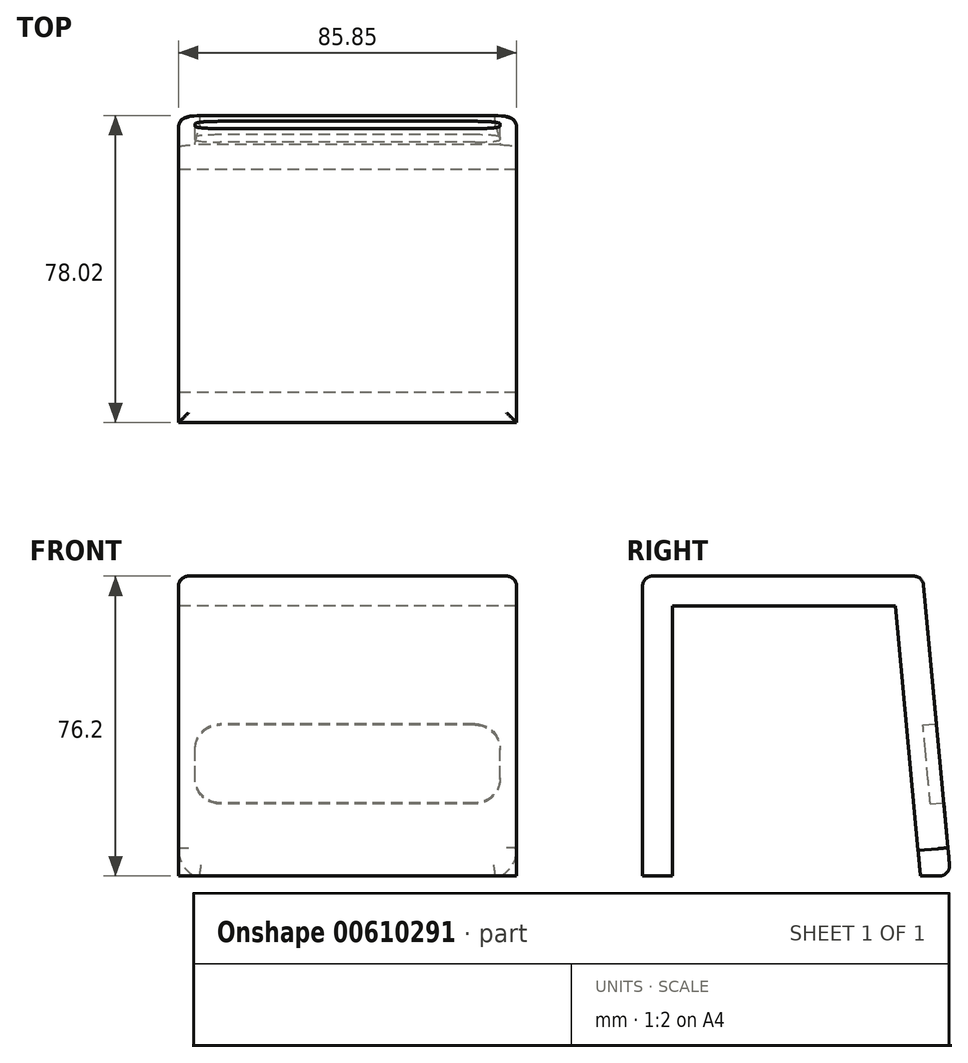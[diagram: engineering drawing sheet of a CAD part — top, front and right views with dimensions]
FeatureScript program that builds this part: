
annotation { "Feature Type Name" : "Feature", "Feature Type Description" : "" }
export const myFeature = defineFeature(function(context is Context, id is Id, definition is map)
    precondition{}
    {
        {
            var Q0;
            Q0=qCreatedBy(makeId("Right.planeOp"),FACE);
            var sketch = newSketch(context, id + "F0", { "sketchPlane" : qUnion([Q0])});
            skLineSegment(sketch, "E0", {"start": v(0, 0) * mm, "end": v(0, 76.2) * mm});
            skLineSegment(sketch, "E1", {"start": v(0, 76.2) * mm, "end": v(71.2, 76.2) * mm});
            skLineSegment(sketch, "E2", {"start": v(71.2, 76.2) * mm, "end": v(78.26, 0) * mm});
            skLineSegment(sketch, "E3", {"start": v(78.26, 0) * mm, "end": v(70.61, 0) * mm});
            skLineSegment(sketch, "E4", {"start": v(70.61, 0) * mm, "end": v(64.26, 68.58) * mm});
            skLineSegment(sketch, "E5", {"start": v(64.26, 68.58) * mm, "end": v(7.62, 68.58) * mm});
            skLineSegment(sketch, "E6", {"start": v(7.62, 68.58) * mm, "end": v(7.62, 0) * mm});
            skLineSegment(sketch, "E7", {"start": v(7.62, 0) * mm, "end": v(0, 0) * mm});
            skSolve(sketch);
        }
        {
            var Q0;
            Q0 = qSketchRegion(id + "F0", true);
            extrude(context, id + "F1", {"entities" : qUnion([Q0]), "depth" : 85.85 * mm, "offsetDistance" : 25.4 * mm});
        }
        {
            var Q0;
            Q0=makeQuery(id+"F1.opExtrude","SWEPT_FACE",FACE,{"disambiguationData":[OSD([sQuery(id+"F0.wireOp",EDGE,"E2")])]});
            var sketch = newSketch(context, id + "F2", { "sketchPlane" : qUnion([Q0])});
            skLineSegment(sketch, "E8.bottom", {"start": v(-75.31, 11.46) * mm, "end": v(-10.54, 11.46) * mm});
            skLineSegment(sketch, "E8.top", {"start": v(-75.31, 31.63) * mm, "end": v(-10.54, 31.63) * mm});
            skLineSegment(sketch, "E8.left", {"start": v(-81.66, 17.81) * mm, "end": v(-81.66, 25.28) * mm});
            skLineSegment(sketch, "E8.right", {"start": v(-4.2, 17.81) * mm, "end": v(-4.2, 25.28) * mm});
            skPoint(sketch, "E9.visualSharp", {"position": v(-4.2, 31.63) * mm});
            skArc(sketch, "E9.filletArc", {"start": v(-4.2, 25.28) * mm, "mid": v(-6.05, 29.77) * mm, "end": v(-10.54, 31.63) * mm});
            skPoint(sketch, "E10.visualSharp", {"position": v(-4.2, 11.46) * mm});
            skArc(sketch, "E10.filletArc", {"start": v(-10.54, 11.46) * mm, "mid": v(-6.05, 13.32) * mm, "end": v(-4.2, 17.81) * mm});
            skPoint(sketch, "E11.visualSharp", {"position": v(-81.66, 11.46) * mm});
            skArc(sketch, "E11.filletArc", {"start": v(-81.66, 17.81) * mm, "mid": v(-79.8, 13.32) * mm, "end": v(-75.31, 11.46) * mm});
            skPoint(sketch, "E12.visualSharp", {"position": v(-81.66, 31.63) * mm});
            skArc(sketch, "E12.filletArc", {"start": v(-75.31, 31.63) * mm, "mid": v(-79.8, 29.77) * mm, "end": v(-81.66, 25.28) * mm});
            skArc(sketch, "E13.0", {"start": v(-75.31, 32.42) * mm, "mid": v(-80.36, 30.33) * mm, "end": v(-82.45, 25.28) * mm});
            skLineSegment(sketch, "E13.1", {"start": v(-82.45, 17.81) * mm, "end": v(-82.45, 25.28) * mm});
            skLineSegment(sketch, "E13.2", {"start": v(-75.31, 32.42) * mm, "end": v(-10.54, 32.42) * mm});
            skArc(sketch, "E13.3", {"start": v(-82.45, 17.81) * mm, "mid": v(-80.36, 12.76) * mm, "end": v(-75.31, 10.67) * mm});
            skArc(sketch, "E13.4", {"start": v(-3.4, 25.28) * mm, "mid": v(-5.49, 30.33) * mm, "end": v(-10.54, 32.42) * mm});
            skLineSegment(sketch, "E13.5", {"start": v(-3.4, 17.81) * mm, "end": v(-3.4, 25.28) * mm});
            skArc(sketch, "E13.6", {"start": v(-10.54, 10.67) * mm, "mid": v(-5.49, 12.76) * mm, "end": v(-3.4, 17.81) * mm});
            skLineSegment(sketch, "E13.7", {"start": v(-75.31, 10.67) * mm, "end": v(-10.54, 10.67) * mm});
            skSolve(sketch);
        }
        {
            var Q0;
            Q0=makeQuery(id+"F2.imprint","IMPRINT",FACE,{"disambiguationData":[TD([[makeQuery(id+"F2.imprint","IMPRINT",EDGE,{"derivedFrom":sQuery(id+"F2.wireOp",EDGE,"E8.bottom")}),1.0]])]});
            extrude(context, id + "F3", {"entities" : qUnion([Q0]), "operationType" : NewBodyOperationType.REMOVE, "oppositeDirection" : true, "depth" : 3.43 * mm, "offsetDistance" : 25.4 * mm});
        }
        {
            var Q0;
            Q0=makeQuery(id+"F1.opExtrude","SWEPT_FACE",FACE,{"disambiguationData":[OSD([sQuery(id+"F0.wireOp",EDGE,"E2")])]});
            var sketch = newSketch(context, id + "F4", { "sketchPlane" : qUnion([Q0])});
            skArc(sketch, "E14", {"start": v(-85.85, 0) * mm, "mid": v(-83.83, -4.97) * mm, "end": v(-78.97, -7.22) * mm});
            skLineSegment(sketch, "E15", {"start": v(-85.85, 0) * mm, "end": v(-85.85, -7.22) * mm});
            skLineSegment(sketch, "E16", {"start": v(-85.85, -7.22) * mm, "end": v(-78.97, -7.22) * mm});
            skLineSegment(sketch, "E17", {"start": v(-42.93, -7.22) * mm, "end": v(-42.93, 0) * mm});
            skArc(sketch, "E18.MirrorCS", {"start": v(0, 0) * mm, "mid": v(-2.02, -4.97) * mm, "end": v(-6.88, -7.22) * mm});
            skLineSegment(sketch, "E19.MirrorCS", {"start": v(0, 0) * mm, "end": v(0, -7.22) * mm});
            skLineSegment(sketch, "E20.MirrorCS", {"start": v(0, -7.22) * mm, "end": v(-6.88, -7.22) * mm});
            skSolve(sketch);
        }
        {
            var Q0;
            Q0 = qSketchRegion(id + "F4", true);
            extrude(context, id + "F5", {"entities" : qUnion([Q0]), "operationType" : NewBodyOperationType.REMOVE, "oppositeDirection" : true, "depth" : 25.4 * mm, "offsetDistance" : 25.4 * mm});
        }
        {
            var Q0;
            Q0=makeQuery(id+"F1.opExtrude","CAP_EDGE",EDGE,{"disambiguationData":[OSD([sQuery(id+"F0.wireOp",EDGE,"E1")])],"isStart":false});
            var Q1;
            Q1=makeQuery(id+"F1.opExtrude","SWEPT_EDGE",EDGE,{"disambiguationData":[OSD([sQuery(id+"F0.wireOp",EDGE,"E1"),sQuery(id+"F0.wireOp",EDGE,"E2")])]});
            var Q2;
            Q2=makeQuery(id+"F1.opExtrude","CAP_EDGE",EDGE,{"disambiguationData":[OSD([sQuery(id+"F0.wireOp",EDGE,"E2")])],"isStart":false});
            var Q3;
            Q3=makeQuery(id+"F1.opExtrude","SWEPT_EDGE",EDGE,{"disambiguationData":[OSD([sQuery(id+"F0.wireOp",EDGE,"E2"),sQuery(id+"F0.wireOp",EDGE,"E3")])]});
            var Q4;
            Q4=makeQuery(id+"F1.opExtrude","CAP_EDGE",EDGE,{"disambiguationData":[OSD([sQuery(id+"F0.wireOp",EDGE,"E2")])],"isStart":true});
            var Q5;
            Q5=makeQuery(id+"F1.opExtrude","SWEPT_FACE",FACE,{"disambiguationData":[OSD([sQuery(id+"F0.wireOp",EDGE,"E1")])]});
            fillet(context, id + "F6", {"entities" : qUnion([Q0, Q1, Q2, Q3, Q4, Q5]), "radius" : 2.54 * mm, "tangentPropagation" : true, "allowEdgeOverflow" : false});
        }
    });
